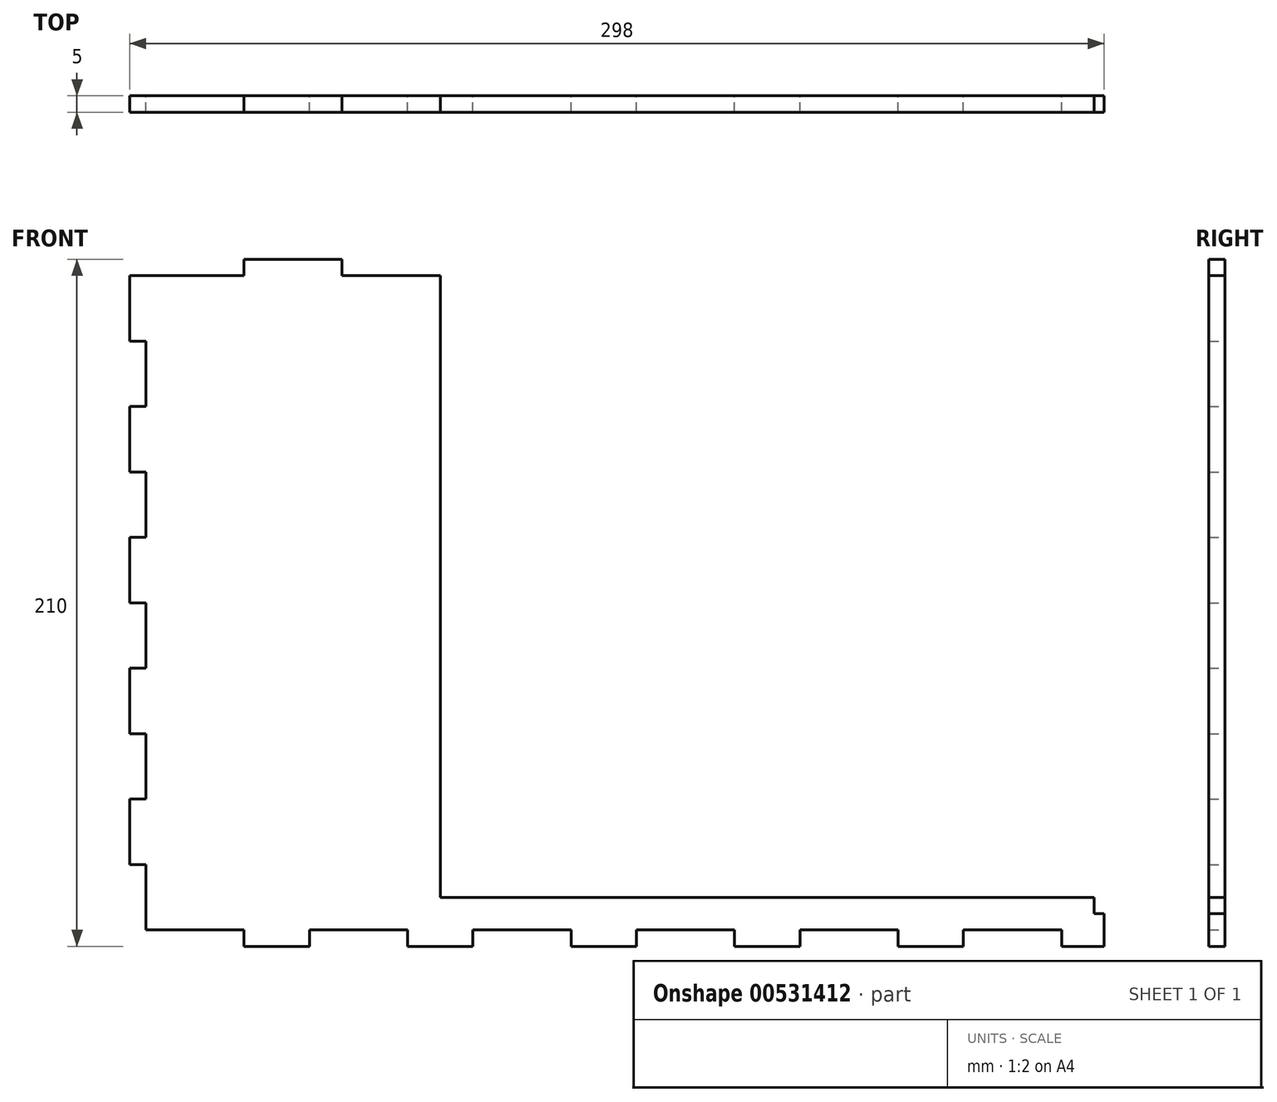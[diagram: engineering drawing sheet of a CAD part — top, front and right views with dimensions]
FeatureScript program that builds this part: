
annotation { "Feature Type Name" : "Feature", "Feature Type Description" : "" }
export const myFeature = defineFeature(function(context is Context, id is Id, definition is map)
    precondition{}
    {
        {
            var Q0;
            Q0=qCreatedBy(makeId("Front.planeOp"),FACE);
            var sketch = newSketch(context, id + "F0", { "sketchPlane" : qUnion([Q0])});
            skLineSegment(sketch, "E0", {"start": v(0, 163.79) * mm, "end": v(-30, 163.79) * mm});
            skLineSegment(sketch, "E1", {"start": v(-90, 143.79) * mm, "end": v(-90, 123.79) * mm});
            skLineSegment(sketch, "E2", {"start": v(-90, -36.21) * mm, "end": v(-60, -36.21) * mm});
            skLineSegment(sketch, "E3", {"start": v(200, -31.21) * mm, "end": v(200, -26.21) * mm});
            skLineSegment(sketch, "E4", {"start": v(200, -26.21) * mm, "end": v(0, -26.21) * mm});
            skLineSegment(sketch, "E5", {"start": v(0, -26.21) * mm, "end": v(0, 163.79) * mm});
            skLineSegment(sketch, "E6", {"start": v(0, 163.79) * mm, "end": v(0, 168.79) * mm, "construction": true});
            skLineSegment(sketch, "E7", {"start": v(0, 168.79) * mm, "end": v(-95, 168.79) * mm, "construction": true});
            skLineSegment(sketch, "E8", {"start": v(-95, 168.79) * mm, "end": v(-95, -41.21) * mm, "construction": true});
            skLineSegment(sketch, "E9", {"start": v(-95, -41.21) * mm, "end": v(199.87, -41.21) * mm, "construction": true});
            skLineSegment(sketch, "E10", {"start": v(-60, 163.79) * mm, "end": v(-60, 168.79) * mm});
            skLineSegment(sketch, "E11", {"start": v(-60, 168.79) * mm, "end": v(-30, 168.79) * mm});
            skLineSegment(sketch, "E12", {"start": v(-30, 168.79) * mm, "end": v(-30, 163.79) * mm});
            skLineSegment(sketch, "E13.trimOffspring", {"start": v(-60, 163.79) * mm, "end": v(-90, 163.79) * mm});
            skLineSegment(sketch, "E14", {"start": v(-90, 163.79) * mm, "end": v(-95, 163.79) * mm});
            skLineSegment(sketch, "E15", {"start": v(-95, 163.79) * mm, "end": v(-95, 143.79) * mm});
            skLineSegment(sketch, "E16", {"start": v(-95, 143.79) * mm, "end": v(-90, 143.79) * mm});
            skLineSegment(sketch, "E17", {"start": v(-90, 123.79) * mm, "end": v(-95, 123.79) * mm});
            skLineSegment(sketch, "E18", {"start": v(-95, 123.79) * mm, "end": v(-95, 103.79) * mm});
            skLineSegment(sketch, "E19", {"start": v(-95, 103.79) * mm, "end": v(-90, 103.79) * mm});
            skLineSegment(sketch, "E20", {"start": v(-90, 83.79) * mm, "end": v(-95, 83.79) * mm});
            skLineSegment(sketch, "E21", {"start": v(-95, 83.79) * mm, "end": v(-95, 63.79) * mm});
            skLineSegment(sketch, "E22", {"start": v(-95, 63.79) * mm, "end": v(-90, 63.79) * mm});
            skLineSegment(sketch, "E23", {"start": v(-90, 63.79) * mm, "end": v(0, 63.79) * mm, "construction": true});
            skLineSegment(sketch, "E24.MirrorCS", {"start": v(-95, -41.21) * mm, "end": v(-95, 168.79) * mm, "construction": true});
            skLineSegment(sketch, "E25.MirrorCS", {"start": v(-90, 43.79) * mm, "end": v(-95, 43.79) * mm});
            skLineSegment(sketch, "E26.MirrorCS", {"start": v(-95, 23.79) * mm, "end": v(-90, 23.79) * mm});
            skLineSegment(sketch, "E27.MirrorCS", {"start": v(-90, 3.79) * mm, "end": v(-95, 3.79) * mm});
            skLineSegment(sketch, "E28.MirrorCS", {"start": v(-95, -16.21) * mm, "end": v(-90, -16.21) * mm});
            skLineSegment(sketch, "E29", {"start": v(-95, 43.79) * mm, "end": v(-95, 23.79) * mm});
            skLineSegment(sketch, "E30", {"start": v(-95, 3.79) * mm, "end": v(-95, -16.21) * mm});
            skPoint(sketch, "E31.MirrorCS.end.orphan", {"position": v(-95, -36.21) * mm});
            skPoint(sketch, "E31.MirrorCS.start.orphan", {"position": v(-90, -36.21) * mm});
            skLineSegment(sketch, "E32.trimOffspring", {"start": v(-90, -16.21) * mm, "end": v(-90, -36.21) * mm});
            skLineSegment(sketch, "E33.trimOffspring", {"start": v(-90, 23.79) * mm, "end": v(-90, 3.79) * mm});
            skLineSegment(sketch, "E34.trimOffspring", {"start": v(-90, 63.79) * mm, "end": v(-90, 43.79) * mm});
            skLineSegment(sketch, "E35.trimOffspring", {"start": v(-90, 103.79) * mm, "end": v(-90, 83.79) * mm});
            skLineSegment(sketch, "E36", {"start": v(-60, -36.21) * mm, "end": v(-60, -41.21) * mm});
            skLineSegment(sketch, "E37", {"start": v(-60, -41.21) * mm, "end": v(-40, -41.21) * mm});
            skLineSegment(sketch, "E38", {"start": v(-40, -41.21) * mm, "end": v(-40, -36.21) * mm});
            skLineSegment(sketch, "E39", {"start": v(-10, -36.21) * mm, "end": v(-10, -41.21) * mm});
            skLineSegment(sketch, "E40", {"start": v(-10, -41.21) * mm, "end": v(10, -41.21) * mm});
            skLineSegment(sketch, "E41", {"start": v(10, -41.21) * mm, "end": v(10, -36.21) * mm});
            skLineSegment(sketch, "E42", {"start": v(10, -36.21) * mm, "end": v(40, -36.21) * mm});
            skLineSegment(sketch, "E43", {"start": v(40, -36.21) * mm, "end": v(40, -41.21) * mm});
            skLineSegment(sketch, "E44", {"start": v(40, -41.21) * mm, "end": v(60, -41.21) * mm});
            skLineSegment(sketch, "E45", {"start": v(60, -41.21) * mm, "end": v(60, -36.21) * mm});
            skLineSegment(sketch, "E46", {"start": v(60, -36.21) * mm, "end": v(90, -36.21) * mm});
            skLineSegment(sketch, "E47", {"start": v(90, -36.21) * mm, "end": v(90, -41.21) * mm});
            skLineSegment(sketch, "E48", {"start": v(90, -41.21) * mm, "end": v(110, -41.21) * mm});
            skLineSegment(sketch, "E49", {"start": v(110, -41.21) * mm, "end": v(110, -36.21) * mm});
            skLineSegment(sketch, "E50", {"start": v(110, -36.21) * mm, "end": v(140, -36.21) * mm});
            skLineSegment(sketch, "E51", {"start": v(140, -36.21) * mm, "end": v(140, -41.21) * mm});
            skLineSegment(sketch, "E52", {"start": v(140, -41.21) * mm, "end": v(160, -41.21) * mm});
            skLineSegment(sketch, "E53", {"start": v(160, -41.21) * mm, "end": v(160, -36.21) * mm});
            skLineSegment(sketch, "E54", {"start": v(160, -36.21) * mm, "end": v(190, -36.21) * mm});
            skLineSegment(sketch, "E55", {"start": v(190, -36.21) * mm, "end": v(190, -41.21) * mm});
            skLineSegment(sketch, "E56", {"start": v(190, -41.21) * mm, "end": v(194.22, -41.21) * mm});
            skLineSegment(sketch, "E57", {"start": v(194.22, -41.21) * mm, "end": v(199.87, -41.21) * mm});
            skLineSegment(sketch, "E58", {"start": v(200, -41.21) * mm, "end": v(190, -41.21) * mm});
            skLineSegment(sketch, "E59.trimOffspring", {"start": v(-40, -36.21) * mm, "end": v(-10, -36.21) * mm});
            skLineSegment(sketch, "E60", {"start": v(200, -26.21) * mm, "end": v(203, -26.21) * mm, "construction": true});
            skLineSegment(sketch, "E61", {"start": v(203, -26.21) * mm, "end": v(203, -41.21) * mm, "construction": true});
            skLineSegment(sketch, "E62", {"start": v(203, -41.21) * mm, "end": v(200, -41.21) * mm, "construction": true});
            skLineSegment(sketch, "E63", {"start": v(200, -31.21) * mm, "end": v(203, -31.21) * mm});
            skLineSegment(sketch, "E64", {"start": v(203, -31.21) * mm, "end": v(203, -41.21) * mm});
            skLineSegment(sketch, "E65", {"start": v(200, -41.21) * mm, "end": v(203, -41.21) * mm});
            skPoint(sketch, "E66.start.orphan", {"position": v(200, -36.21) * mm});
            skSolve(sketch);
        }
        {
            var Q0;
            Q0 = qSketchRegion(id + "F0", true);
            extrude(context, id + "F1", {"entities" : qUnion([Q0]), "depth" : 5 * mm, "offsetDistance" : 25 * mm});
        }
    });
